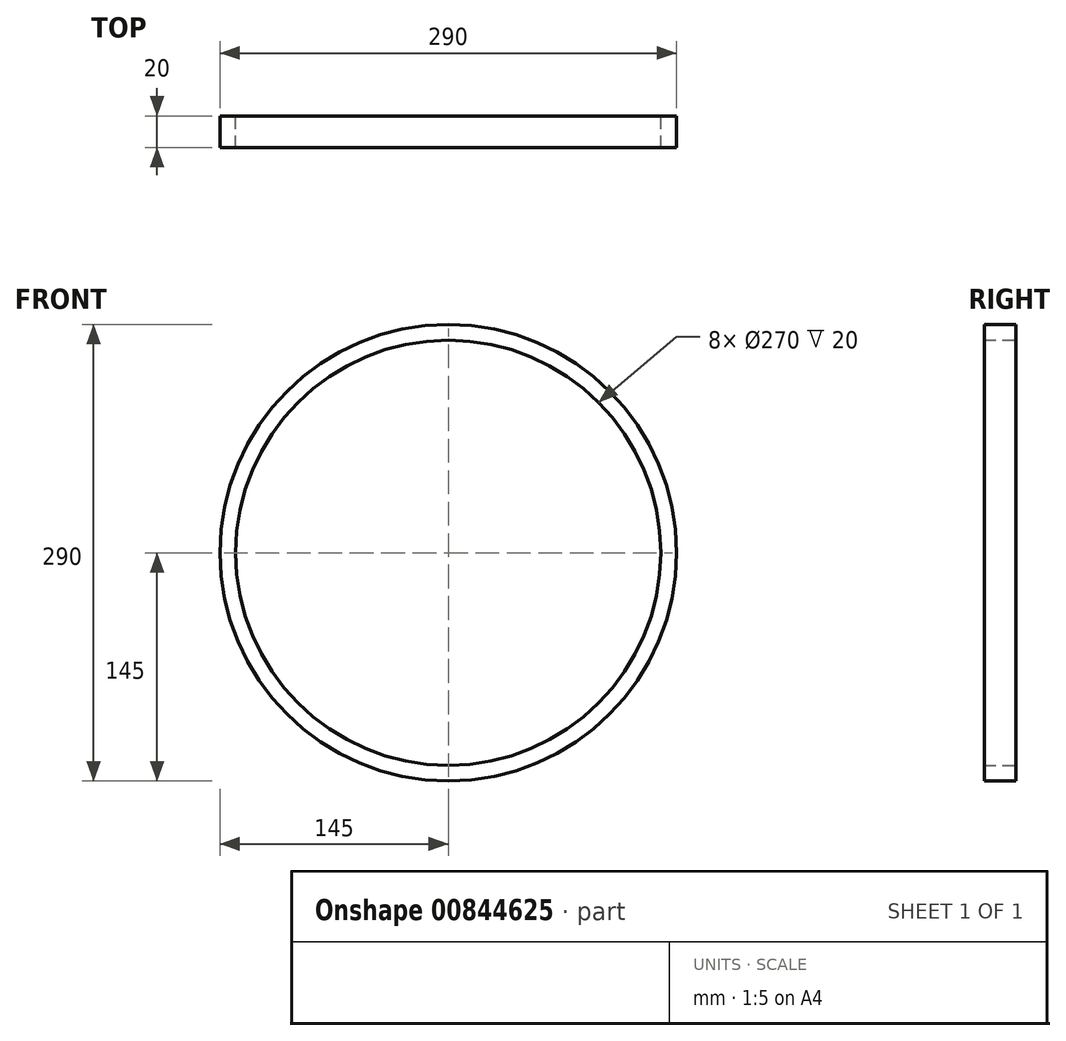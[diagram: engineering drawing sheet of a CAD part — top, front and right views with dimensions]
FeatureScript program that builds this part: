
annotation { "Feature Type Name" : "Feature", "Feature Type Description" : "" }
export const myFeature = defineFeature(function(context is Context, id is Id, definition is map)
    precondition{}
    {
        {
            var Q0;
            Q0=qCreatedBy(makeId("Front.planeOp"),FACE);
            var sketch = newSketch(context, id + "F0", { "sketchPlane" : qUnion([Q0])});
            skCircle(sketch, "E0", {"center": v(0, 0) * mm, "radius": 145 * mm});
            skCircle(sketch, "E1", {"center": v(0, 0) * mm, "radius": 135 * mm});
            skSolve(sketch);
        }
        {
            var Q0;
            Q0=makeQuery(id+"F0.imprint","IMPRINT",FACE,{"disambiguationData":[TD([[makeQuery(id+"F0.imprint","IMPRINT",EDGE,{"derivedFrom":sQuery(id+"F0.wireOp",EDGE,"E0")}),1.0]])]});
            extrude(context, id + "F1", {"entities" : qUnion([Q0]), "depth" : 20 * mm, "offsetDistance" : 25 * mm});
        }
    });
